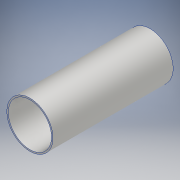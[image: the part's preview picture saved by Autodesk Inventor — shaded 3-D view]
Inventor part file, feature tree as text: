
AUTODESK INVENTOR PART (.ipt)
format: ipt  version: 2018 (Build 220112000, 112)  size: 100,352 bytes
history: native  units: mm
features: other x1, extrude x1, sketch x1
ambient origin geometry x8: Origin, YZ Plane, XZ Plane, XY Plane, X Axis, Y Axis, Z Axis, Center Point
bodies: Body1 (feature_tree)
feature tree (3):
  other  "ソリッド1"
  extrude  "押し出し1"  Depth=90.0mm
  sketch  "スケッチ1"
